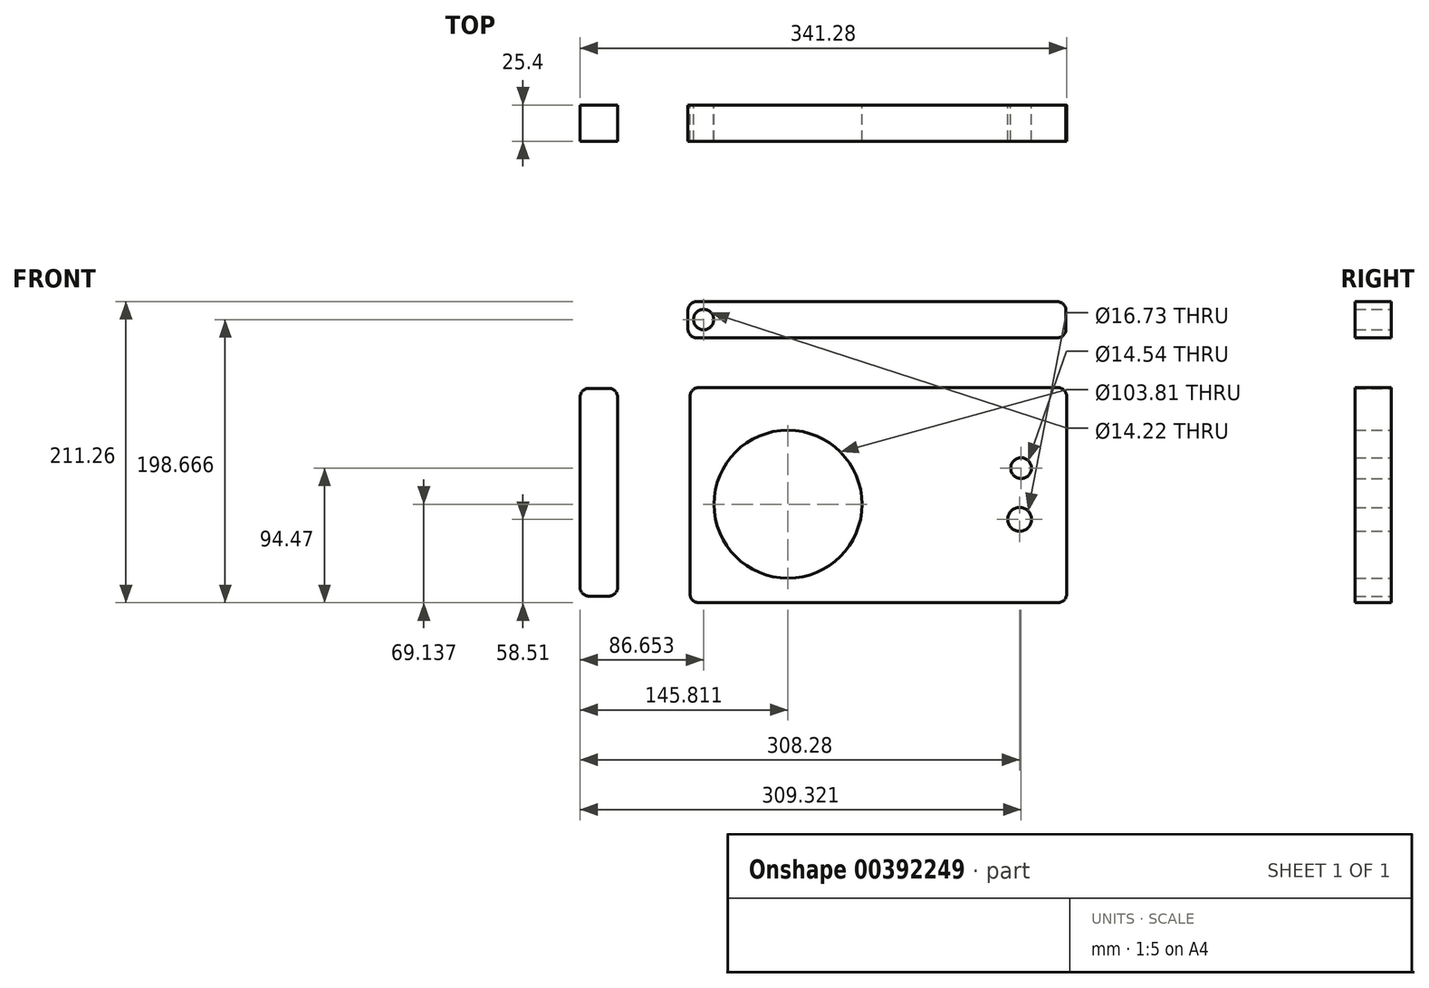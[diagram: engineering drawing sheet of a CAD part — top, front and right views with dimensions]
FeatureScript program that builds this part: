
annotation { "Feature Type Name" : "Feature", "Feature Type Description" : "" }
export const myFeature = defineFeature(function(context is Context, id is Id, definition is map)
    precondition{}
    {
        {
            var Q0;
            Q0=qCreatedBy(makeId("Front.planeOp"),FACE);
            var sketch = newSketch(context, id + "F0", { "sketchPlane" : qUnion([Q0])});
            skCircle(sketch, "E0", {"center": v(-33.36, 10.63) * mm, "radius": 49.92 * mm});
            skLineSegment(sketch, "E1.bottom", {"start": v(-95.78, -58.51) * mm, "end": v(155.76, -58.51) * mm});
            skLineSegment(sketch, "E1.top", {"start": v(-95.78, 92.52) * mm, "end": v(155.76, 92.52) * mm});
            skLineSegment(sketch, "E1.left", {"start": v(-102.13, -52.16) * mm, "end": v(-102.13, 86.17) * mm});
            skLineSegment(sketch, "E1.right", {"start": v(162.1, -52.16) * mm, "end": v(162.1, 86.17) * mm});
            skCircle(sketch, "E2", {"center": v(130.15, 35.96) * mm, "radius": 7.27 * mm});
            skCircle(sketch, "E3", {"center": v(129.1, 0) * mm, "radius": 8.37 * mm});
            skLineSegment(sketch, "E4.bottom", {"start": v(-159.17, 91.94) * mm, "end": v(-172.82, 91.94) * mm});
            skLineSegment(sketch, "E4.top", {"start": v(-159.17, -53.81) * mm, "end": v(-172.82, -53.81) * mm});
            skLineSegment(sketch, "E4.left", {"start": v(-152.82, 85.59) * mm, "end": v(-152.82, -47.46) * mm});
            skLineSegment(sketch, "E4.right", {"start": v(-179.17, 85.59) * mm, "end": v(-179.17, -47.46) * mm});
            skLineSegment(sketch, "E5.bottom", {"start": v(-97.21, 127.27) * mm, "end": v(155.27, 127.27) * mm});
            skLineSegment(sketch, "E5.top", {"start": v(-97.21, 152.75) * mm, "end": v(155.27, 152.75) * mm});
            skLineSegment(sketch, "E5.left", {"start": v(-103.56, 133.62) * mm, "end": v(-103.56, 146.4) * mm});
            skLineSegment(sketch, "E5.right", {"start": v(161.62, 133.62) * mm, "end": v(161.62, 146.4) * mm});
            skCircle(sketch, "E6", {"center": v(-92.52, 140.16) * mm, "radius": 7.11 * mm});
            skLineSegment(sketch, "E7", {"start": v(-91.96, 92.52) * mm, "end": v(-91.96, -51.84) * mm, "construction": true});
            skLineSegment(sketch, "E8", {"start": v(-91.96, -51.84) * mm, "end": v(-91.96, -58.51) * mm, "construction": true});
            skPoint(sketch, "E9.visualSharp", {"position": v(162.1, 92.52) * mm});
            skArc(sketch, "E9.filletArc", {"start": v(162.1, 86.17) * mm, "mid": v(160.25, 90.66) * mm, "end": v(155.76, 92.52) * mm});
            skPoint(sketch, "E10.visualSharp", {"position": v(162.1, -58.51) * mm});
            skArc(sketch, "E10.filletArc", {"start": v(155.76, -58.51) * mm, "mid": v(160.25, -56.65) * mm, "end": v(162.1, -52.16) * mm});
            skPoint(sketch, "E11.visualSharp", {"position": v(-102.13, -58.51) * mm});
            skArc(sketch, "E11.filletArc", {"start": v(-102.13, -52.16) * mm, "mid": v(-100.27, -56.65) * mm, "end": v(-95.78, -58.51) * mm});
            skPoint(sketch, "E12.visualSharp", {"position": v(-102.13, 92.52) * mm});
            skArc(sketch, "E12.filletArc", {"start": v(-95.78, 92.52) * mm, "mid": v(-100.27, 90.66) * mm, "end": v(-102.13, 86.17) * mm});
            skPoint(sketch, "E13.visualSharp", {"position": v(-103.56, 127.27) * mm});
            skArc(sketch, "E13.filletArc", {"start": v(-103.56, 133.62) * mm, "mid": v(-101.7, 129.13) * mm, "end": v(-97.21, 127.27) * mm});
            skPoint(sketch, "E14.visualSharp", {"position": v(-103.56, 152.75) * mm});
            skArc(sketch, "E14.filletArc", {"start": v(-97.21, 152.75) * mm, "mid": v(-101.7, 150.9) * mm, "end": v(-103.56, 146.4) * mm});
            skPoint(sketch, "E15.visualSharp", {"position": v(161.62, 152.75) * mm});
            skArc(sketch, "E15.filletArc", {"start": v(161.62, 146.4) * mm, "mid": v(159.77, 150.9) * mm, "end": v(155.27, 152.75) * mm});
            skPoint(sketch, "E16.visualSharp", {"position": v(161.62, 127.27) * mm});
            skArc(sketch, "E16.filletArc", {"start": v(155.27, 127.27) * mm, "mid": v(159.77, 129.13) * mm, "end": v(161.62, 133.62) * mm});
            skPoint(sketch, "E17.visualSharp", {"position": v(-152.82, -53.81) * mm});
            skArc(sketch, "E17.filletArc", {"start": v(-159.17, -53.81) * mm, "mid": v(-154.68, -51.95) * mm, "end": v(-152.82, -47.46) * mm});
            skPoint(sketch, "E18.visualSharp", {"position": v(-152.82, 91.94) * mm});
            skArc(sketch, "E18.filletArc", {"start": v(-152.82, 85.59) * mm, "mid": v(-154.68, 90.08) * mm, "end": v(-159.17, 91.94) * mm});
            skPoint(sketch, "E19.visualSharp", {"position": v(-179.17, 91.94) * mm});
            skArc(sketch, "E19.filletArc", {"start": v(-172.82, 91.94) * mm, "mid": v(-177.3, 90.08) * mm, "end": v(-179.17, 85.59) * mm});
            skPoint(sketch, "E20.visualSharp", {"position": v(-179.17, -53.81) * mm});
            skArc(sketch, "E20.filletArc", {"start": v(-179.17, -47.46) * mm, "mid": v(-177.3, -51.95) * mm, "end": v(-172.82, -53.81) * mm});
            skCircle(sketch, "E21", {"center": v(-33.36, 10.63) * mm, "radius": 51.9 * mm});
            skLineSegment(sketch, "E22", {"start": v(-102.13, 17) * mm, "end": v(-84.87, 17) * mm});
            skPoint(sketch, "E22.endSnap0", {"position": v(-102.13, 17) * mm});
            skLineSegment(sketch, "E23", {"start": v(-84.87, 17) * mm, "end": v(-102.13, 17) * mm});
            skSolve(sketch);
        }
        {
            var Q0;
            Q0 = qSketchRegion(id + "F0", true);
            extrude(context, id + "F1", {"entities" : qUnion([Q0]), "depth" : 25.4 * mm});
        }
    });
